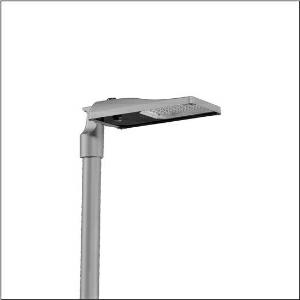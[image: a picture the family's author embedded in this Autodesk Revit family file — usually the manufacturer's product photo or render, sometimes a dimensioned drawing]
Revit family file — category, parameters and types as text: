
# Revit family: streetlight_sl_31_mini___st1_0a_5xh6d71t08ha_56cc
name_source: partatom
category: Lighting Fixtures
units: mm (PartAtom-declared; Revit-internal decimal feet)

## family parameters
Cut with Voids When Loaded = No
Host = Face
Light Source = No
Part Type = Normal
Room Calculation Point = No
Round Connector Dimension = Use Diameter
Shared = No

## types (1)
- --- (1 x LED, 7620 lm, 68.3 W, 2200K)
    Apparent Load = 68 VA
    CIE Flux Codes = 37 72 97 100 100
    Color Rendering = 70
    Color Temperature = 2200K
    Default Elevation = 1800 mm
    Description = Streetlight SL 31 mini D4i, Desk-Remote mast luminaire for post-top, side-entry; light control with lens of PMMA; light distribution: ST1.0a, direct asymmetric distribution, for standard-compliant lighting for roads and squares; LED: luminous flux: 7.620lm, light colour: 722, colour temperature: 2200K; luminous efficacy: 111,7lm/W; control: pre-setting: logarithmic dimming characteristic, flexible luminous flux parameterisation, time-dependent luminous flux control, constant luminous flux control, power reduction, intelligent temperature release in ECG and LED module, overheat protection; luminaire housing, of diecast aluminium, Siteco® metallic grey (DB 702S), corrosivity category C5 high according to DIN EN ISO 12944; cover of toughened safety glass, transparent, opened without tools; mast flange of diecast aluminium, Siteco® metallic grey (DB 702S), spigot size: 76/60mm, mast flange included unmounted; with cable H07RN-F 2x 1.5mm², cable length: 8,5m, connection cable pre-assembled; mains connection: 220..240V, AC, 50/60Hz; power consumption (at start of service life): 68,2W / (at end of service life): 74,4W / (with reduced operation 50%): 29,4W; protection rating (complete): IP66; insulation class (complete): insulation class II (safety insulation); impact resistance: IK09; certification: CE, ENEC, ENEC+, VDE, UKCA, ZD4i; permissible operating ambient temperature for outdoor applications: -40..+50°C; packaging unit: 1 piece

Light Distribution: ST1.0a
    Height = 76 mm
    Lamp = 1 x LED
    Lamp Light Flux = 7620 lm
    Lamp Power = 68.3 W
    Lamp count = 1
    Length = 547 mm
    Luminous efficacy = 112 lm/W
    Manufacturer = Siteco
    ModVariant = No
    Model = 5XH6D71T08HA
    Number of Poles = 1
    OnlyDefault = Yes
    Power Factor = 1
    Product Name = Streetlight SL 31 mini | ST1.0a
    Product group = mast luminaire | pylon top
    ProductGroupID = 6100
    Protection Class = Protection class II
    Protection Degree = IP 66
    RLX_Detail_Level = 1
    RLX_Emergency_Light_Flux = 0 lm
    RLX_Emergency_Type = 0
    RLX_Emergency_Type_DB = No
    RlxData = <blob elided: 24313 chars, md5=aa3bf566>
    Socket = socket
    Standby Power = 0 W
    System Light Flux = 7620 lm
    System Power = 68 W
    Type Comments = factory setting: luminous flux: 100 % | dim-lin: 254 | 692 mA
    Type Image = l_1300332.jpg
    URL = http://relux.com
    VarID = @adj_002425
    Voltage = 0 V
    Weight = 0.00 kg
    Width = 265 mm

## geometry (parser evidence)
native form markers: Blend x4, Sweep x11
no freeform markers — native parametric forms only
